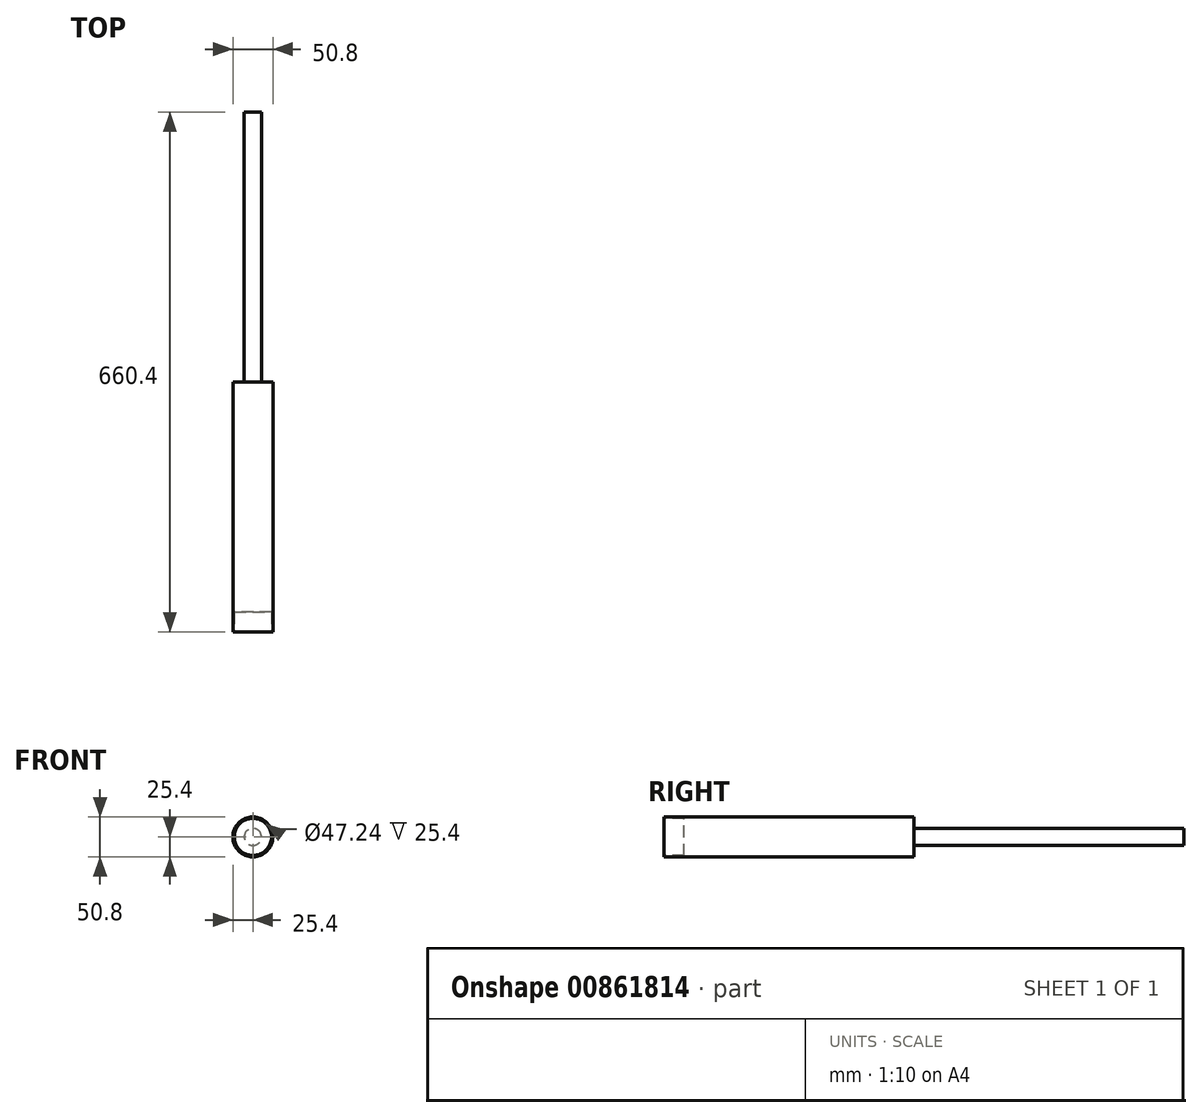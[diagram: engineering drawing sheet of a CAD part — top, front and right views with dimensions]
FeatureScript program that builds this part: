
annotation { "Feature Type Name" : "Feature", "Feature Type Description" : "" }
export const myFeature = defineFeature(function(context is Context, id is Id, definition is map)
    precondition{}
    {
        {
            var Q0;
            Q0=qCreatedBy(makeId("Front.planeOp"),FACE);
            var sketch = newSketch(context, id + "F0", { "sketchPlane" : qUnion([Q0])});
            skCircle(sketch, "E0", {"center": v(0, 0) * mm, "radius": 25.4 * mm});
            skSolve(sketch);
        }
        {
            var Q0;
            Q0=makeQuery(id+"F0.imprint","IMPRINT",FACE,{"disambiguationData":[TD([[makeQuery(id+"F0.imprint","IMPRINT",EDGE,{"derivedFrom":sQuery(id+"F0.wireOp",EDGE,"E0")}),1.0]])]});
            extrude(context, id + "F1", {"entities" : qUnion([Q0]), "depth" : 317.5 * mm, "offsetDistance" : 25.4 * mm});
        }
        {
            var Q0;
            Q0=makeQuery(id+"F1.opExtrude","CAP_FACE",FACE,{"disambiguationData":[OSD([sQuery(id+"F0.wireOp",EDGE,"E0")])],"isStart":false});
            var sketch = newSketch(context, id + "F2", { "sketchPlane" : qUnion([Q0])});
            skCircle(sketch, "E1", {"center": v(0, 0) * mm, "radius": 23.62 * mm});
            skSolve(sketch);
        }
        {
            var Q0;
            Q0 = qSketchRegion(id + "F2", true);
            extrude(context, id + "F3", {"entities" : qUnion([Q0]), "operationType" : NewBodyOperationType.REMOVE, "oppositeDirection" : true, "depth" : 25.4 * mm, "offsetDistance" : 25.4 * mm});
        }
        {
            var Q0;
            Q0=qCreatedBy(makeId("Front.planeOp"),FACE);
            var sketch = newSketch(context, id + "F4", { "sketchPlane" : qUnion([Q0])});
            skCircle(sketch, "E2", {"center": v(0, 0) * mm, "radius": 10.92 * mm});
            skSolve(sketch);
        }
        {
            var Q0;
            Q0 = qSketchRegion(id + "F4", true);
            extrude(context, id + "F5", {"entities" : qUnion([Q0]), "operationType" : NewBodyOperationType.ADD, "oppositeDirection" : true, "depth" : 342.9 * mm, "offsetDistance" : 25.4 * mm});
        }
    });
